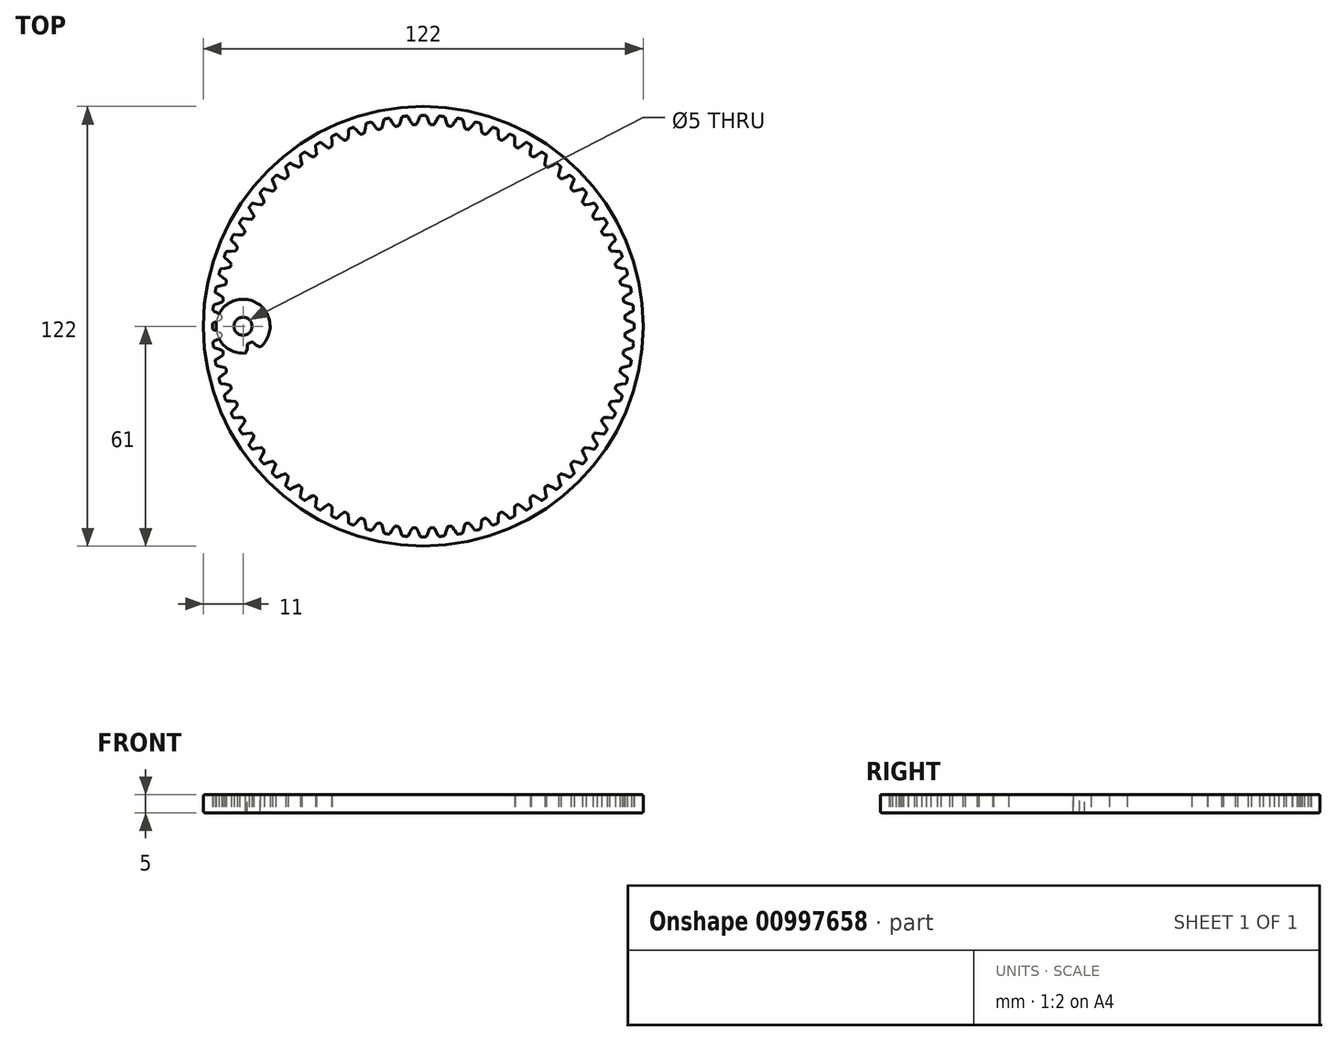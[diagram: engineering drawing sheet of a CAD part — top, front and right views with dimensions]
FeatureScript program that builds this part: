
annotation { "Feature Type Name" : "Feature", "Feature Type Description" : "" }
export const myFeature = defineFeature(function(context is Context, id is Id, definition is map)
    precondition{}
    {
        {
            var Q0;
            Q0=qCreatedBy(makeId("Top.planeOp"),FACE);
            var sketch = newSketch(context, id + "F0", { "sketchPlane" : qUnion([Q0])});
            skCircle(sketch, "E0", {"center": v(0, 0) * mm, "radius": 2.5 * mm});
            skCircle(sketch, "E1", {"center": v(0, 0) * mm, "radius": 7.5 * mm});
            skSolve(sketch);
        }
        {
            var Q0;
            Q0 = qSketchRegion(id + "F0", true);
            extrude(context, id + "F1", {"entities" : qUnion([Q0]), "depth" : 5 * mm, "offsetDistance" : 25 * mm});
        }
        {
            var Q0;
            Q0=makeQuery(id+"F1.opExtrude","CAP_FACE",FACE,{"disambiguationData":[OSD([sQuery(id+"F0.wireOp",EDGE,"E0"),sQuery(id+"F0.wireOp",EDGE,"E1")])],"isStart":false});
            var sketch = newSketch(context, id + "F2", { "sketchPlane" : qUnion([Q0])});
            skCircle(sketch, "E2", {"center": v(0, 0) * mm, "radius": 7.5 * mm});
            skCircle(sketch, "E3", {"center": v(0, 0) * mm, "radius": 5 * mm});
            skLineSegment(sketch, "E4", {"start": v(0, 0) * mm, "end": v(0, -7.5) * mm});
            skLineSegment(sketch, "E5", {"start": v(0, 0) * mm, "end": v(1.17, -7.4) * mm});
            skCircle(sketch, "E6", {"center": v(0, 0) * mm, "radius": 6.25 * mm});
            skLineSegment(sketch, "E7", {"start": v(0.78, -4.94) * mm, "end": v(1.26, -6.12) * mm});
            skLineSegment(sketch, "E8", {"start": v(1.26, -6.12) * mm, "end": v(2.23, -7.16) * mm});
            skLineSegment(sketch, "E9", {"start": v(1.26, -6.12) * mm, "end": v(1.73, -7.3) * mm});
            skLineSegment(sketch, "E10.MirrorCS", {"start": v(0, 0) * mm, "end": v(-1.17, -7.4) * mm});
            skLineSegment(sketch, "E11.MirrorCS", {"start": v(-0.78, -4.94) * mm, "end": v(-1.26, -6.12) * mm});
            skLineSegment(sketch, "E12.MirrorCS", {"start": v(-1.26, -6.12) * mm, "end": v(-2.23, -7.16) * mm});
            skSolve(sketch);
        }
        {
            var Q0;
            {var subQ0=sQuery(id+"F2.wireOp",EDGE,"E4");var subQ1=sQuery(id+"F2.wireOp",EDGE,"E2");var subQ2=makeQuery(id+"F2.imprint","INTERSECT",VERTEX,{"derivedFrom":[subQ1,subQ0]});Q0=makeQuery(id+"F2.imprint","IMPRINT",FACE,{"disambiguationData":[TD([[makeQuery(id+"F2.imprint","IMPRINT",EDGE,{"disambiguationData":[TD([[subQ2,1.0]])],"derivedFrom":subQ1}),1.0]])]});}
            var Q1;
            {var subQ0=sQuery(id+"F2.wireOp",EDGE,"E4");var subQ1=sQuery(id+"F2.wireOp",EDGE,"E2");var subQ2=makeQuery(id+"F2.imprint","INTERSECT",VERTEX,{"derivedFrom":[subQ1,subQ0]});Q1=makeQuery(id+"F2.imprint","IMPRINT",FACE,{"disambiguationData":[TD([[makeQuery(id+"F2.imprint","IMPRINT",EDGE,{"disambiguationData":[TD([[subQ2,-1.0]])],"derivedFrom":subQ1}),1.0]])]});}
            var Q2;
            {var subQ1=sQuery(id+"F2.wireOp",EDGE,"E3");var subQ3=sQuery(id+"F2.wireOp",EDGE,"E4");var subQ4=makeQuery(id+"F2.imprint","INTERSECT",VERTEX,{"derivedFrom":[subQ1,subQ3]});Q2=makeQuery(id+"F2.imprint","IMPRINT",FACE,{"disambiguationData":[TD([[makeQuery(id+"F2.imprint","IMPRINT",EDGE,{"disambiguationData":[TD([[subQ4,-1.0]])],"derivedFrom":subQ3}),1.0]])]});}
            var Q3;
            {var subQ1=sQuery(id+"F2.wireOp",EDGE,"E3");var subQ3=sQuery(id+"F2.wireOp",EDGE,"E4");var subQ4=makeQuery(id+"F2.imprint","INTERSECT",VERTEX,{"derivedFrom":[subQ1,subQ3]});Q3=makeQuery(id+"F2.imprint","IMPRINT",FACE,{"disambiguationData":[TD([[makeQuery(id+"F2.imprint","IMPRINT",EDGE,{"disambiguationData":[TD([[subQ4,-1.0]])],"derivedFrom":subQ3}),-1.0]])]});}
            var Q4;
            {var subQ0=sQuery(id+"F2.wireOp",EDGE,"E11.MirrorCS");Q4=makeQuery(id+"F2.imprint","IMPRINT",FACE,{"disambiguationData":[TD([[makeQuery(id+"F2.imprint","IMPRINT",EDGE,{"derivedFrom":subQ0}),1.0]])]});}
            var Q5;
            {var subQ3=sQuery(id+"F2.wireOp",EDGE,"E12.MirrorCS");Q5=makeQuery(id+"F2.imprint","IMPRINT",FACE,{"disambiguationData":[TD([[makeQuery(id+"F2.imprint","IMPRINT",EDGE,{"derivedFrom":subQ3}),1.0]])]});}
            var Q6;
            {var subQ0=sQuery(id+"F2.wireOp",EDGE,"E7");Q6=makeQuery(id+"F2.imprint","IMPRINT",FACE,{"disambiguationData":[TD([[makeQuery(id+"F2.imprint","IMPRINT",EDGE,{"derivedFrom":subQ0}),-1.0]])]});}
            var Q7;
            {var subQ3=sQuery(id+"F2.wireOp",EDGE,"E9");Q7=makeQuery(id+"F2.imprint","IMPRINT",FACE,{"disambiguationData":[TD([[makeQuery(id+"F2.imprint","IMPRINT",EDGE,{"derivedFrom":subQ3}),-1.0]])]});}
            var Q8;
            {var subQ0=sQuery(id+"F2.wireOp",EDGE,"E8");Q8=makeQuery(id+"F2.imprint","IMPRINT",FACE,{"disambiguationData":[TD([[makeQuery(id+"F2.imprint","IMPRINT",EDGE,{"derivedFrom":subQ0}),-1.0]])]});}
            extrude(context, id + "F3", {"entities" : qUnion([Q0, Q1, Q2, Q3, Q4, Q5, Q6, Q7, Q8]), "operationType" : NewBodyOperationType.REMOVE, "oppositeDirection" : true, "depth" : 25 * mm, "offsetDistance" : 25 * mm});
        }
        {
            var Q0;
            Q0=makeQuery(id+"F3.boolean.opBoolean","COPY",EDGE,{"derivedFrom":makeQuery(id+"F3.opExtrude","SWEPT_EDGE",EDGE,{"disambiguationData":[OSD([sQuery(id+"F2.wireOp",EDGE,"E2"),sQuery(id+"F2.wireOp",EDGE,"E12.MirrorCS")])]})});
            var Q1;
            Q1=makeQuery(id+"F3.boolean.opBoolean","COPY",EDGE,{"derivedFrom":makeQuery(id+"F3.opExtrude","SWEPT_EDGE",EDGE,{"disambiguationData":[OSD([sQuery(id+"F2.wireOp",EDGE,"E6"),sQuery(id+"F2.wireOp",EDGE,"E11.MirrorCS"),sQuery(id+"F2.wireOp",EDGE,"E12.MirrorCS")])]})});
            var Q2;
            Q2=makeQuery(id+"F3.boolean.opBoolean","COPY",EDGE,{"derivedFrom":makeQuery(id+"F3.opExtrude","SWEPT_EDGE",EDGE,{"disambiguationData":[OSD([sQuery(id+"F2.wireOp",EDGE,"E3"),sQuery(id+"F2.wireOp",EDGE,"E10.MirrorCS"),sQuery(id+"F2.wireOp",EDGE,"E11.MirrorCS")])]})});
            var Q3;
            Q3=makeQuery(id+"F3.boolean.opBoolean","COPY",EDGE,{"derivedFrom":makeQuery(id+"F3.opExtrude","SWEPT_EDGE",EDGE,{"disambiguationData":[OSD([sQuery(id+"F2.wireOp",EDGE,"E3"),sQuery(id+"F2.wireOp",EDGE,"E5"),sQuery(id+"F2.wireOp",EDGE,"E7")])]})});
            var Q4;
            Q4=makeQuery(id+"F3.boolean.opBoolean","COPY",EDGE,{"derivedFrom":makeQuery(id+"F3.opExtrude","SWEPT_EDGE",EDGE,{"disambiguationData":[OSD([sQuery(id+"F2.wireOp",EDGE,"E6"),sQuery(id+"F2.wireOp",EDGE,"E7"),sQuery(id+"F2.wireOp",EDGE,"E8"),sQuery(id+"F2.wireOp",EDGE,"E9")])]})});
            var Q5;
            Q5=makeQuery(id+"F3.boolean.opBoolean","COPY",EDGE,{"derivedFrom":makeQuery(id+"F3.opExtrude","SWEPT_EDGE",EDGE,{"disambiguationData":[OSD([sQuery(id+"F2.wireOp",EDGE,"E2"),sQuery(id+"F2.wireOp",EDGE,"E8")])]})});
            fillet(context, id + "F4", {"entities" : qUnion([Q0, Q1, Q2, Q3, Q4, Q5]), "radius" : .5 * mm, "tangentPropagation" : true, "allowEdgeOverflow" : false});
        }
        {
            var Q0;
            {var subQ0=sQuery(id+"F0.wireOp",EDGE,"E1");var subQ4=sQuery(id+"F2.wireOp",EDGE,"E8");Q0=makeQuery(id+"F0W0TyMPhCpBQsk_1.7.F3.boolean.opBoolean","SPLIT",EDGE,{"disambiguationData":[TD([makeQuery(id+"F0W0TyMPhCpBQsk_1.7.F3.opExtrude","SWEPT_FACE",FACE,{"disambiguationData":[OSD([subQ4])]})])],"derivedFrom":makeQuery(id+"F0W0TyMPhCpBQsk_1.6.F3.boolean.opBoolean","SPLIT",EDGE,{"disambiguationData":[TD([makeQuery(id+"F0W0TyMPhCpBQsk_1.6.F3.opExtrude","SWEPT_FACE",FACE,{"disambiguationData":[OSD([subQ4])]})])],"derivedFrom":makeQuery(id+"F0W0TyMPhCpBQsk_1.5.F3.boolean.opBoolean","SPLIT",EDGE,{"disambiguationData":[TD([makeQuery(id+"F0W0TyMPhCpBQsk_1.5.F3.opExtrude","SWEPT_FACE",FACE,{"disambiguationData":[OSD([subQ4])]})])],"derivedFrom":makeQuery(id+"F0W0TyMPhCpBQsk_1.4.F3.boolean.opBoolean","SPLIT",EDGE,{"disambiguationData":[TD([makeQuery(id+"F0W0TyMPhCpBQsk_1.4.F3.opExtrude","SWEPT_FACE",FACE,{"disambiguationData":[OSD([subQ4])]})])],"derivedFrom":makeQuery(id+"F0W0TyMPhCpBQsk_1.3.F3.boolean.opBoolean","SPLIT",EDGE,{"disambiguationData":[TD([makeQuery(id+"F0W0TyMPhCpBQsk_1.3.F3.opExtrude","SWEPT_FACE",FACE,{"disambiguationData":[OSD([subQ4])]})])],"derivedFrom":makeQuery(id+"F0W0TyMPhCpBQsk_1.2.F3.boolean.opBoolean","SPLIT",EDGE,{"disambiguationData":[TD([makeQuery(id+"F0W0TyMPhCpBQsk_1.2.F3.opExtrude","SWEPT_FACE",FACE,{"disambiguationData":[OSD([subQ4])]})])],"derivedFrom":makeQuery(id+"F0W0TyMPhCpBQsk_1.1.F3.boolean.opBoolean","SPLIT",EDGE,{"disambiguationData":[TD([makeQuery(id+"F0W0TyMPhCpBQsk_1.1.F3.opExtrude","SWEPT_FACE",FACE,{"disambiguationData":[OSD([subQ4])]})])],"derivedFrom":makeQuery(id+"F1.opExtrude","CAP_EDGE",EDGE,{"disambiguationData":[OSD([subQ0])],"isStart":false})})})})})})})});}
            var Q1;
            {var subQ0=sQuery(id+"F0.wireOp",EDGE,"E1");var subQ4=sQuery(id+"F2.wireOp",EDGE,"E8");Q1=makeQuery(id+"F0W0TyMPhCpBQsk_1.7.F3.boolean.opBoolean","SPLIT",EDGE,{"disambiguationData":[TD([makeQuery(id+"F0W0TyMPhCpBQsk_1.7.F3.opExtrude","SWEPT_FACE",FACE,{"disambiguationData":[OSD([subQ4])]})])],"derivedFrom":makeQuery(id+"F0W0TyMPhCpBQsk_1.6.F3.boolean.opBoolean","SPLIT",EDGE,{"disambiguationData":[TD([makeQuery(id+"F0W0TyMPhCpBQsk_1.6.F3.opExtrude","SWEPT_FACE",FACE,{"disambiguationData":[OSD([subQ4])]})])],"derivedFrom":makeQuery(id+"F0W0TyMPhCpBQsk_1.5.F3.boolean.opBoolean","SPLIT",EDGE,{"disambiguationData":[TD([makeQuery(id+"F0W0TyMPhCpBQsk_1.5.F3.opExtrude","SWEPT_FACE",FACE,{"disambiguationData":[OSD([subQ4])]})])],"derivedFrom":makeQuery(id+"F0W0TyMPhCpBQsk_1.4.F3.boolean.opBoolean","SPLIT",EDGE,{"disambiguationData":[TD([makeQuery(id+"F0W0TyMPhCpBQsk_1.4.F3.opExtrude","SWEPT_FACE",FACE,{"disambiguationData":[OSD([subQ4])]})])],"derivedFrom":makeQuery(id+"F0W0TyMPhCpBQsk_1.3.F3.boolean.opBoolean","SPLIT",EDGE,{"disambiguationData":[TD([makeQuery(id+"F0W0TyMPhCpBQsk_1.3.F3.opExtrude","SWEPT_FACE",FACE,{"disambiguationData":[OSD([subQ4])]})])],"derivedFrom":makeQuery(id+"F0W0TyMPhCpBQsk_1.2.F3.boolean.opBoolean","SPLIT",EDGE,{"disambiguationData":[TD([makeQuery(id+"F0W0TyMPhCpBQsk_1.2.F3.opExtrude","SWEPT_FACE",FACE,{"disambiguationData":[OSD([subQ4])]})])],"derivedFrom":makeQuery(id+"F0W0TyMPhCpBQsk_1.1.F3.boolean.opBoolean","SPLIT",EDGE,{"disambiguationData":[TD([makeQuery(id+"F0W0TyMPhCpBQsk_1.1.F3.opExtrude","SWEPT_FACE",FACE,{"disambiguationData":[OSD([subQ4])]})])],"derivedFrom":makeQuery(id+"F1.opExtrude","CAP_EDGE",EDGE,{"disambiguationData":[OSD([subQ0])],"isStart":true})})})})})})})});}
            var Q2;
            Q2=makeQuery(id+"F1.opExtrude","CAP_EDGE",EDGE,{"disambiguationData":[OSD([sQuery(id+"F0.wireOp",EDGE,"E0")])],"isStart":false});
            var Q3;
            Q3=makeQuery(id+"F1.opExtrude","CAP_EDGE",EDGE,{"disambiguationData":[OSD([sQuery(id+"F0.wireOp",EDGE,"E0")])],"isStart":true});
            fillet(context, id + "F5", {"entities" : qUnion([Q0, Q1, Q2, Q3]), "radius" : .35 * mm, "tangentPropagation" : true, "allowEdgeOverflow" : false});
        }
        {
            var Q0;
            Q0=qCreatedBy(makeId("Top.planeOp"),FACE);
            var sketch = newSketch(context, id + "F6", { "sketchPlane" : qUnion([Q0])});
            skCircle(sketch, "E13", {"center": v(0, 0) * mm, "radius": 56 * mm});
            skCircle(sketch, "E14.0", {"center": v(0, 0) * mm, "radius": 57.25 * mm});
            skCircle(sketch, "E15.0", {"center": v(0, 0) * mm, "radius": 58.5 * mm});
            skCircle(sketch, "E16.0", {"center": v(0, 0) * mm, "radius": 61 * mm});
            skLineSegment(sketch, "E17", {"start": v(0, -56) * mm, "end": v(0, -58.5) * mm});
            skLineSegment(sketch, "E18", {"start": v(0, -58.5) * mm, "end": v(0.8, -58.5) * mm});
            skLineSegment(sketch, "E19", {"start": v(0, -57.24) * mm, "end": v(1.3, -57.24) * mm});
            skLineSegment(sketch, "E20", {"start": v(0, -56) * mm, "end": v(0, -55.97) * mm});
            skLineSegment(sketch, "E21", {"start": v(0, -55.97) * mm, "end": v(1.9, -55.97) * mm});
            skLineSegment(sketch, "E22", {"start": v(0.8, -58.5) * mm, "end": v(1.3, -57.24) * mm});
            skLineSegment(sketch, "E23", {"start": v(1.3, -57.24) * mm, "end": v(1.9, -55.97) * mm});
            skLineSegment(sketch, "E24.MirrorCS", {"start": v(-0.8, -58.5) * mm, "end": v(-1.3, -57.24) * mm});
            skLineSegment(sketch, "E25.MirrorCS", {"start": v(-1.3, -57.24) * mm, "end": v(-1.9, -55.97) * mm});
            skSolve(sketch);
        }
        {
            var Q0;
            Q0=makeQuery(id+"F6.imprint","IMPRINT",FACE,{"disambiguationData":[TD([[makeQuery(id+"F6.imprint","IMPRINT",EDGE,{"derivedFrom":sQuery(id+"F6.wireOp",EDGE,"E15.0")}),-1.0]])]});
            var Q1;
            {var subQ0=sQuery(id+"F6.wireOp",EDGE,"E22");Q1=makeQuery(id+"F6.imprint","IMPRINT",FACE,{"disambiguationData":[TD([[makeQuery(id+"F6.imprint","IMPRINT",EDGE,{"derivedFrom":subQ0}),-1.0]])]});}
            var Q2;
            {var subQ0=sQuery(id+"F6.wireOp",EDGE,"E23");Q2=makeQuery(id+"F6.imprint","IMPRINT",FACE,{"disambiguationData":[TD([[makeQuery(id+"F6.imprint","IMPRINT",EDGE,{"derivedFrom":subQ0}),-1.0]])]});}
            extrude(context, id + "F7", {"entities" : qUnion([Q0, Q1, Q2]), "depth" : 5 * mm, "offsetDistance" : 25 * mm});
        }
        {
            var Q0;
            Q0=makeQuery(id+"F7.opExtrude","SWEPT_EDGE",EDGE,{"disambiguationData":[OSD([sQuery(id+"F6.wireOp",EDGE,"E13"),sQuery(id+"F6.wireOp",EDGE,"E25.MirrorCS")])]});
            var Q1;
            Q1=makeQuery(id+"F7.opExtrude","SWEPT_EDGE",EDGE,{"disambiguationData":[OSD([sQuery(id+"F6.wireOp",EDGE,"E14.0"),sQuery(id+"F6.wireOp",EDGE,"E24.MirrorCS"),sQuery(id+"F6.wireOp",EDGE,"E25.MirrorCS")])]});
            var Q2;
            Q2=makeQuery(id+"F7.opExtrude","SWEPT_EDGE",EDGE,{"disambiguationData":[OSD([sQuery(id+"F6.wireOp",EDGE,"E15.0"),sQuery(id+"F6.wireOp",EDGE,"E24.MirrorCS")])]});
            var Q3;
            Q3=makeQuery(id+"F7.opExtrude","SWEPT_EDGE",EDGE,{"disambiguationData":[OSD([sQuery(id+"F6.wireOp",EDGE,"E15.0"),sQuery(id+"F6.wireOp",EDGE,"E18"),sQuery(id+"F6.wireOp",EDGE,"E22")])]});
            var Q4;
            Q4=makeQuery(id+"F7.opExtrude","SWEPT_EDGE",EDGE,{"disambiguationData":[OSD([sQuery(id+"F6.wireOp",EDGE,"E14.0"),sQuery(id+"F6.wireOp",EDGE,"E19"),sQuery(id+"F6.wireOp",EDGE,"E22"),sQuery(id+"F6.wireOp",EDGE,"E23")])]});
            var Q5;
            Q5=makeQuery(id+"F7.opExtrude","SWEPT_EDGE",EDGE,{"disambiguationData":[OSD([sQuery(id+"F6.wireOp",EDGE,"E13"),sQuery(id+"F6.wireOp",EDGE,"E21"),sQuery(id+"F6.wireOp",EDGE,"E23")])]});
            fillet(context, id + "F8", {"entities" : qUnion([Q0, Q1, Q2, Q3, Q4, Q5]), "radius" : .5 * mm, "tangentPropagation" : true, "allowEdgeOverflow" : false});
        }
        {
            var Q0;
            Q0=makeQuery(id+"F8.opFillet","BLEND_FACE",FACE,{"disambiguationData":[OSD([sQuery(id+"F6.wireOp",EDGE,"E13"),sQuery(id+"F6.wireOp",EDGE,"E25.MirrorCS")])]});
            var Q1;
            Q1=makeQuery(id+"F8.opFillet","BLEND_FACE",FACE,{"disambiguationData":[OSD([sQuery(id+"F6.wireOp",EDGE,"E13"),sQuery(id+"F6.wireOp",EDGE,"E21"),sQuery(id+"F6.wireOp",EDGE,"E23")])]});
            var Q2;
            Q2=makeQuery(id+"F7.opExtrude","SWEPT_FACE",FACE,{"disambiguationData":[OSD([sQuery(id+"F6.wireOp",EDGE,"E23")])]});
            var Q3;
            Q3=makeQuery(id+"F7.opExtrude","SWEPT_FACE",FACE,{"disambiguationData":[OSD([sQuery(id+"F6.wireOp",EDGE,"E25.MirrorCS")])]});
            var Q4;
            Q4=makeQuery(id+"F8.opFillet","BLEND_FACE",FACE,{"disambiguationData":[OSD([sQuery(id+"F6.wireOp",EDGE,"E14.0"),sQuery(id+"F6.wireOp",EDGE,"E24.MirrorCS"),sQuery(id+"F6.wireOp",EDGE,"E25.MirrorCS")])]});
            var Q5;
            Q5=makeQuery(id+"F8.opFillet","BLEND_FACE",FACE,{"disambiguationData":[OSD([sQuery(id+"F6.wireOp",EDGE,"E14.0"),sQuery(id+"F6.wireOp",EDGE,"E19"),sQuery(id+"F6.wireOp",EDGE,"E22"),sQuery(id+"F6.wireOp",EDGE,"E23")])]});
            var Q6;
            Q6=makeQuery(id+"F7.opExtrude","SWEPT_FACE",FACE,{"disambiguationData":[OSD([sQuery(id+"F6.wireOp",EDGE,"E22")])]});
            var Q7;
            Q7=makeQuery(id+"F8.opFillet","BLEND_FACE",FACE,{"disambiguationData":[OSD([sQuery(id+"F6.wireOp",EDGE,"E15.0"),sQuery(id+"F6.wireOp",EDGE,"E18"),sQuery(id+"F6.wireOp",EDGE,"E22")])]});
            var Q8;
            Q8=makeQuery(id+"F7.opExtrude","SWEPT_FACE",FACE,{"disambiguationData":[OSD([sQuery(id+"F6.wireOp",EDGE,"E15.0")])]});
            var Q9;
            Q9=makeQuery(id+"F8.opFillet","BLEND_FACE",FACE,{"disambiguationData":[OSD([sQuery(id+"F6.wireOp",EDGE,"E15.0"),sQuery(id+"F6.wireOp",EDGE,"E24.MirrorCS")])]});
            var Q10;
            Q10=makeQuery(id+"F7.opExtrude","SWEPT_FACE",FACE,{"disambiguationData":[OSD([sQuery(id+"F6.wireOp",EDGE,"E24.MirrorCS")])]});
            var Q11;
            Q11=makeQuery(id+"F7.opExtrude","CAP_EDGE",EDGE,{"disambiguationData":[OSD([sQuery(id+"F6.wireOp",EDGE,"E13")])],"isStart":false});
            circularPattern(context, id + "F9", {"patternType" : PatternType.FACE, "faces" : qUnion([Q0, Q1, Q2, Q3, Q4, Q5, Q6, Q7, Q8, Q9, Q10]), "axis" : qUnion([Q11]), "angle" : 360 * degree, "instanceCount" : 72, "equalSpace" : true});
        }
        {
            var Q0;
            Q0=makeQuery(id+"F9.opPattern","SPLIT",EDGE,{"disambiguationData":[OD(1.0)],"derivedFrom":makeQuery(id+"F7.opExtrude","CAP_EDGE",EDGE,{"disambiguationData":[OSD([sQuery(id+"F6.wireOp",EDGE,"E13")])],"isStart":false})});
            var Q1;
            Q1=makeQuery(id+"F7.opExtrude","CAP_EDGE",EDGE,{"disambiguationData":[OSD([sQuery(id+"F6.wireOp",EDGE,"E16.0")])],"isStart":false});
            var Q2;
            Q2=makeQuery(id+"F7.opExtrude","CAP_EDGE",EDGE,{"disambiguationData":[OSD([sQuery(id+"F6.wireOp",EDGE,"E16.0")])],"isStart":true});
            fillet(context, id + "F10", {"entities" : qUnion([Q0, Q1, Q2]), "radius" : .35 * mm, "tangentPropagation" : true, "allowEdgeOverflow" : false});
        }
        {
            var Q0;
            Q0=makeQuery(id+"F1.opExtrude","SWEPT_BODY",BODY,{"disambiguationData":[OSD([sQuery(id+"F0.wireOp",EDGE,"E0"),sQuery(id+"F0.wireOp",EDGE,"E1")])]});
            var Q1;
            Q1=qCreatedBy(makeId("Right.planeOp"),FACE);
            transform(context, id + "F11", {"entities" : qUnion([Q0]), "transformType" : TransformType.TRANSLATION_DISTANCE, "transformDirection" : qUnion([Q1]), "distance" : 50 * mm, "oppositeDirection" : true, "makeCopy" : false});
        }
        {
            var Q0;
            Q0=makeQuery(id+"F1.opExtrude","SWEPT_BODY",BODY,{"disambiguationData":[OSD([sQuery(id+"F0.wireOp",EDGE,"E0"),sQuery(id+"F0.wireOp",EDGE,"E1")])]});
            var Q1;
            {var subQ0=sQuery(id+"F0.wireOp",EDGE,"E0");Q1=makeQuery(id+"F5.opFillet","BLEND_EDGE",EDGE,{"blendedFrom":[makeQuery(id+"F1.opExtrude","CAP_EDGE",EDGE,{"disambiguationData":[OSD([subQ0])],"isStart":false}),makeQuery(id+"F1.opExtrude","CAP_FACE",FACE,{"disambiguationData":[OSD([subQ0,sQuery(id+"F0.wireOp",EDGE,"E1")])],"isStart":false})],"blendedInto":[makeQuery(id+"F1.opExtrude","CAP_FACE",FACE,{"disambiguationData":[OSD([subQ0,sQuery(id+"F0.wireOp",EDGE,"E1")])],"isStart":false})]});}
            transform(context, id + "F12", {"entities" : qUnion([Q0]), "transformType" : TransformType.ROTATION, "transformAxis" : qUnion([Q1]), "angle" : 22.5 * degree, "makeCopy" : false});
        }
    });
